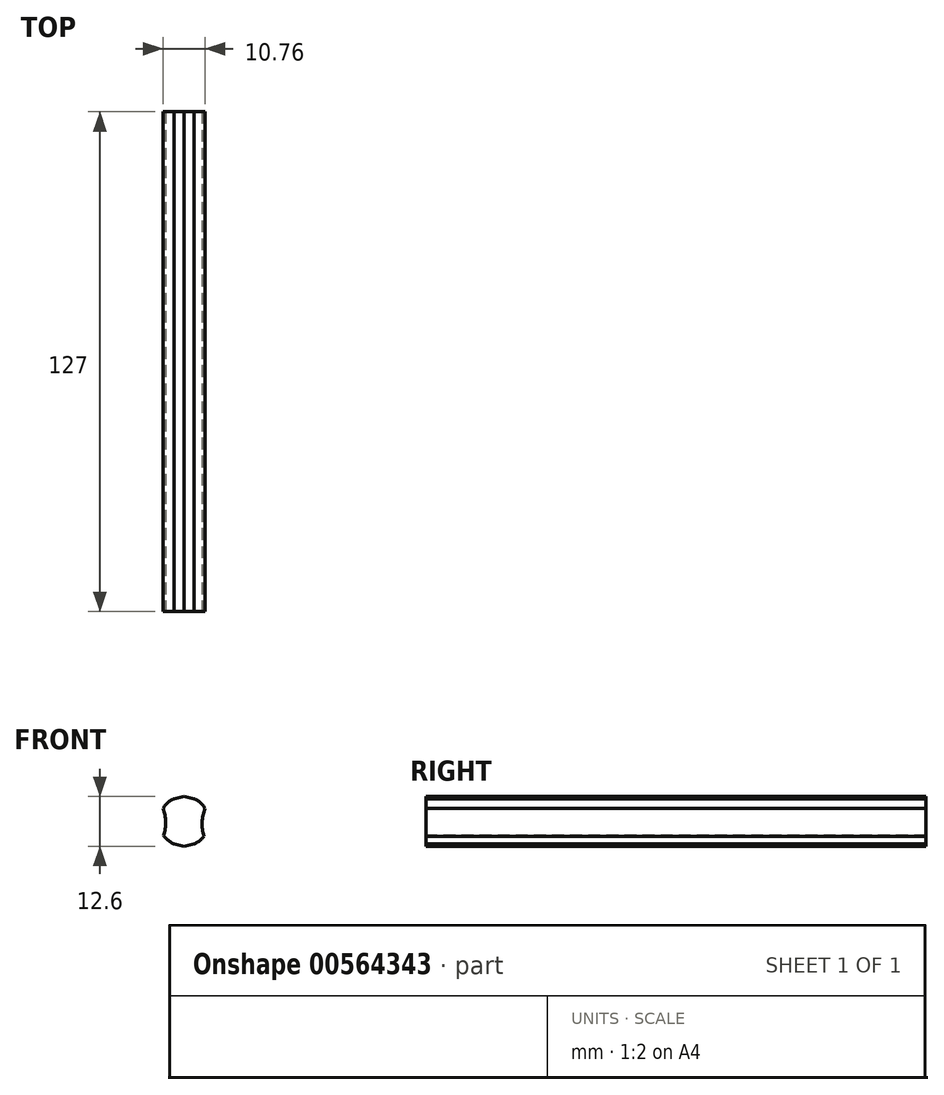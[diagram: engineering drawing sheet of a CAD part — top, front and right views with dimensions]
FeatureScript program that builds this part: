
annotation { "Feature Type Name" : "Feature", "Feature Type Description" : "" }
export const myFeature = defineFeature(function(context is Context, id is Id, definition is map)
    precondition{}
    {
        {
            var Q0;
            Q0=qCreatedBy(makeId("Front.planeOp"),FACE);
            var sketch = newSketch(context, id + "F0", { "sketchPlane" : qUnion([Q0])});
            skArc(sketch, "E0", {"start": v(22.88, -10.72) * mm, "mid": v(21.27, -11.75) * mm, "end": v(20.04, -13.21) * mm});
            skLineSegment(sketch, "E1", {"start": v(25.42, -22.79) * mm, "end": v(27.96, -22.25) * mm});
            skLineSegment(sketch, "E2", {"start": v(27.96, -10.72) * mm, "end": v(25.42, -10.19) * mm});
            skLineSegment(sketch, "E3", {"start": v(25.42, -10.19) * mm, "end": v(22.88, -10.72) * mm});
            skLineSegment(sketch, "E4", {"start": v(22.88, -22.25) * mm, "end": v(25.42, -22.79) * mm});
            skArc(sketch, "E5.trimOffspring", {"start": v(27.96, -22.25) * mm, "mid": v(29.34, -21.41) * mm, "end": v(30.47, -20.25) * mm});
            skArc(sketch, "E6", {"start": v(20.25, -20.08) * mm, "mid": v(20.74, -16.63) * mm, "end": v(20.04, -13.21) * mm});
            skArc(sketch, "E7", {"start": v(30.8, -13.21) * mm, "mid": v(30, -16.7) * mm, "end": v(30.47, -20.25) * mm});
            skArc(sketch, "E8.trimOffspring", {"start": v(30.8, -13.21) * mm, "mid": v(29.57, -11.75) * mm, "end": v(27.96, -10.72) * mm});
            skArc(sketch, "E9.trimOffspring", {"start": v(20.25, -20.08) * mm, "mid": v(21.41, -21.35) * mm, "end": v(22.88, -22.25) * mm});
            skSolve(sketch);
        }
        {
            var Q0;
            Q0=qSketchRegion(id+"F0",true);
            extrude(context, id + "F1", {"entities" : qUnion([Q0]), "oppositeDirection" : true, "depth" : 127 * mm, "offsetDistance" : 25.4 * mm});
        }
    });
